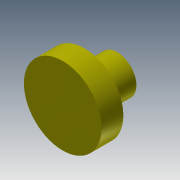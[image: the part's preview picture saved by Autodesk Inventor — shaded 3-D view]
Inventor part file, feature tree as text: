
AUTODESK INVENTOR PART (.ipt)
format: ipt  version: 2013 (Build 170138000, 138)  size: 89,088 bytes
history: native  units: mm
features: extrude x2, sketch x2
ambient origin geometry x8: Origin, YZ Plane, XZ Plane, XY Plane, X Axis, Y Axis, Z Axis, Center Point
bodies: Solid1 (feature_tree)
feature tree (4):
  extrude  "Extrusion1"  Depth=4.0mm TaperAngle=0.0deg
  extrude  "Extrusion2"  Depth=4.0mm
  sketch  "Sketch1"  dims[d0=14.209mm d1=4.0mm d2=0.0mm]
  sketch  "Sketch2"  dims[d3=7.0mm d4=4.0mm d5=6.0mm d6=0.0mm]
